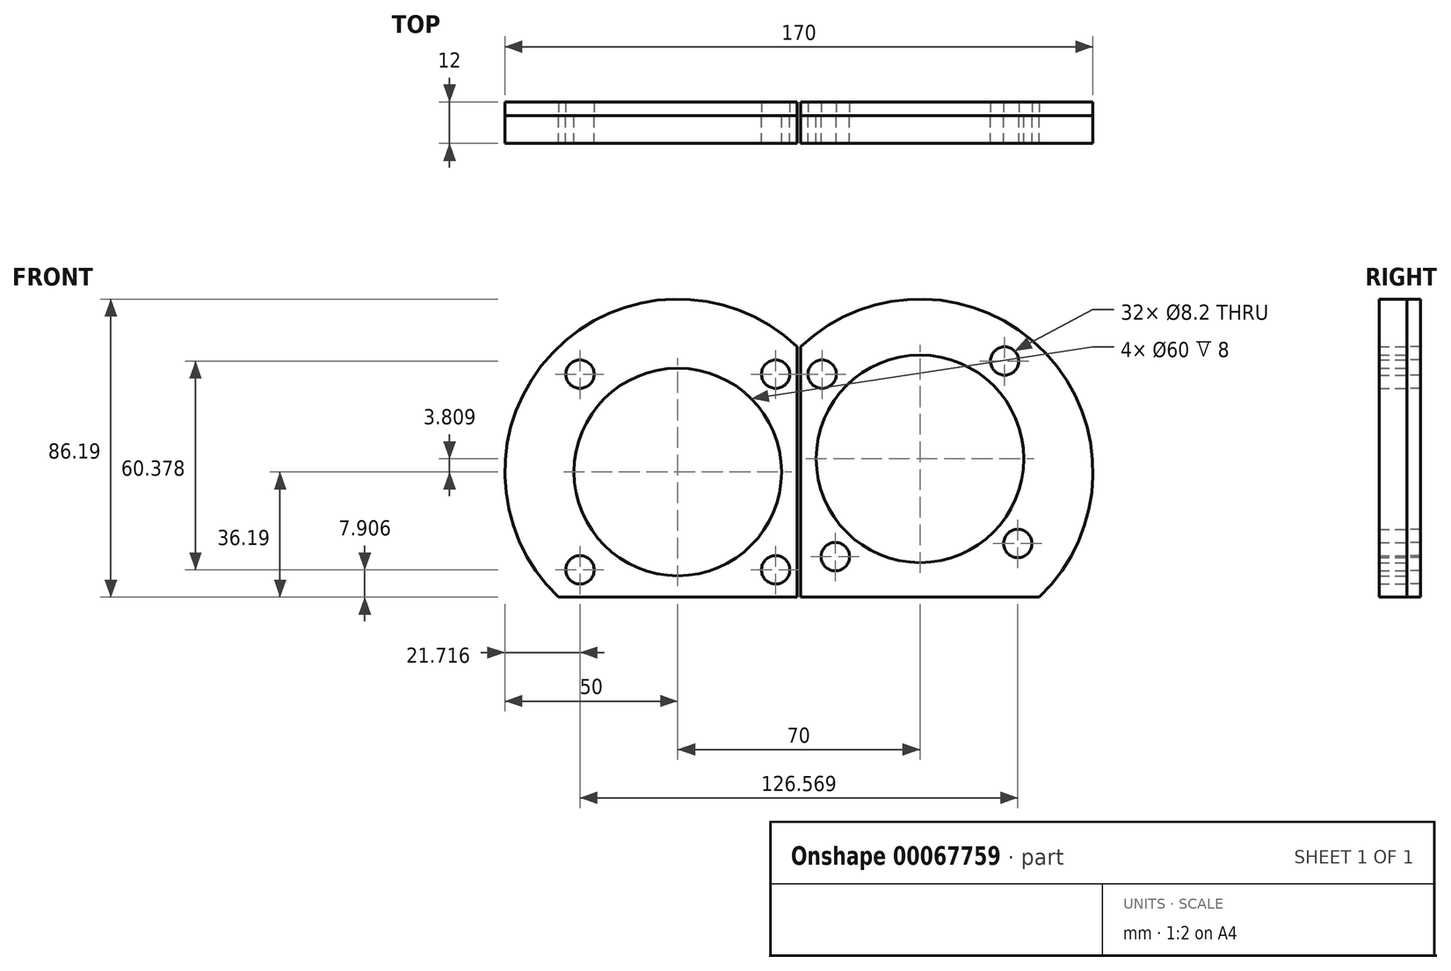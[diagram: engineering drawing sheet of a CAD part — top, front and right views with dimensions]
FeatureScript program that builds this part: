
annotation { "Feature Type Name" : "Feature", "Feature Type Description" : "" }
export const myFeature = defineFeature(function(context is Context, id is Id, definition is map)
    precondition{}
    {
        {
            var Q0;
            Q0=qCreatedBy(makeId("Front.planeOp"),FACE);
            var sketch = newSketch(context, id + "F0", { "sketchPlane" : qUnion([Q0])});
            skCircle(sketch, "E0", {"center": v(-35, 0) * mm, "radius": 30 * mm});
            skArc(sketch, "E1", {"start": v(-0.5, 36.2) * mm, "mid": v(-71.2, 34.5) * mm, "end": v(-69.5, -36.2) * mm});
            skArc(sketch, "E2.trimOffspring", {"start": v(69.5, -36.2) * mm, "mid": v(71.2, 34.5) * mm, "end": v(0.5, 36.2) * mm});
            skCircle(sketch, "E3", {"center": v(35, 3.8) * mm, "radius": 30 * mm});
            skCircle(sketch, "E4.1.0", {"center": v(-63.28, 28.28) * mm, "radius": 4.1 * mm});
            skCircle(sketch, "E4.3.0", {"center": v(-63.28, -28.28) * mm, "radius": 4.1 * mm});
            skCircle(sketch, "E4.5.0", {"center": v(-6.72, -28.28) * mm, "radius": 4.1 * mm});
            skCircle(sketch, "E4.7.0", {"center": v(-6.72, 28.28) * mm, "radius": 4.1 * mm});
            skCircle(sketch, "E5.1.0", {"center": v(6.72, 28.28) * mm, "radius": 4.1 * mm});
            skCircle(sketch, "E6.1.3.0", {"center": v(10.53, -24.47) * mm, "radius": 4.1 * mm});
            skCircle(sketch, "E6.1.5.0", {"center": v(63.28, -20.67) * mm, "radius": 4.1 * mm});
            skCircle(sketch, "E6.1.7.0", {"center": v(59.47, 32.1) * mm, "radius": 4.1 * mm});
            skLineSegment(sketch, "E7.0", {"start": v(-0.5, 36.2) * mm, "end": v(-0.5, -36.2) * mm});
            skLineSegment(sketch, "E8.0", {"start": v(0.5, 36.2) * mm, "end": v(0.5, -36.2) * mm});
            skLineSegment(sketch, "E9", {"start": v(0.5, -36.2) * mm, "end": v(69.5, -36.2) * mm});
            skLineSegment(sketch, "E10", {"start": v(69.5, -36.2) * mm, "end": v(0.5, -36.2) * mm});
            skLineSegment(sketch, "E11.trimOffspring", {"start": v(-0.5, -36.2) * mm, "end": v(-69.5, -36.2) * mm});
            skSolve(sketch);
        }
        {
            var Q0;
            Q0=makeQuery(id+"F0.imprint","IMPRINT",FACE,{"disambiguationData":[TD([[makeQuery(id+"F0.imprint","IMPRINT",EDGE,{"derivedFrom":sQuery(id+"F0.wireOp",EDGE,"E0")}),-1.0]])]});
            var Q1;
            Q1=makeQuery(id+"F0.imprint","IMPRINT",FACE,{"disambiguationData":[TD([[makeQuery(id+"F0.imprint","IMPRINT",EDGE,{"derivedFrom":sQuery(id+"F0.wireOp",EDGE,"E2.trimOffspring")}),1.0]])]});
            extrude(context, id + "F1", {"entities" : qUnion([Q0, Q1]), "depth" : 8 * mm});
        }
        {
            var Q0;
            Q0=makeQuery(id+"F0.imprint","IMPRINT",FACE,{"disambiguationData":[TD([[makeQuery(id+"F0.imprint","IMPRINT",EDGE,{"derivedFrom":sQuery(id+"F0.wireOp",EDGE,"E0")}),-1.0]])]});
            var Q1;
            Q1=makeQuery(id+"F0.imprint","IMPRINT",FACE,{"disambiguationData":[TD([[makeQuery(id+"F0.imprint","IMPRINT",EDGE,{"derivedFrom":sQuery(id+"F0.wireOp",EDGE,"E0")}),1.0]])]});
            extrude(context, id + "F2", {"entities" : qUnion([Q0, Q1]), "oppositeDirection" : true, "depth" : 4 * mm});
        }
        {
            var Q0;
            Q0=makeQuery(id+"F0.imprint","IMPRINT",FACE,{"disambiguationData":[TD([[makeQuery(id+"F0.imprint","IMPRINT",EDGE,{"derivedFrom":sQuery(id+"F0.wireOp",EDGE,"E2.trimOffspring")}),1.0]])]});
            var Q1;
            Q1=makeQuery(id+"F0.imprint","IMPRINT",FACE,{"disambiguationData":[TD([[makeQuery(id+"F0.imprint","IMPRINT",EDGE,{"derivedFrom":sQuery(id+"F0.wireOp",EDGE,"E3")}),1.0]])]});
            extrude(context, id + "F3", {"entities" : qUnion([Q0, Q1]), "oppositeDirection" : true, "depth" : 4 * mm});
        }
    });
